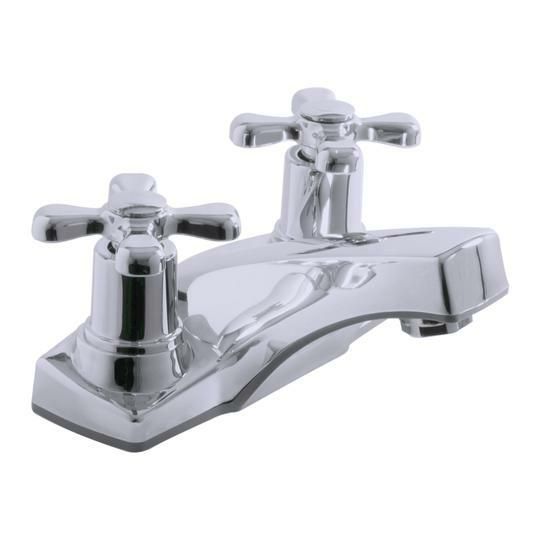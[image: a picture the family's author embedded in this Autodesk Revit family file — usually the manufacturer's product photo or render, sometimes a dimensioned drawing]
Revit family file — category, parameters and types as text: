
# Revit family: 01-1302-11 MEZCLADOR LAVAMANOS 4” ATLANTICO
name_source: partatom
category: Plumbing Fixtures
revit_build: Autodesk Revit 2018 (Build: 20170223_1515(x64)
units: mm (PartAtom-declared; Revit-internal decimal feet)

## family parameters
Cut with Voids When Loaded = No
Host = Face
OmniClass Number = 23.31.11.00
Part Type = Normal
Room Calculation Point = No
Round Connector Dimension = Use Diameter
Shared = No

## types (1)
- 01-1302-11
    Alto = 74.6 mm  [stored 0.244751 ft]
    CW Connection = Yes
    Default Elevation = 0 mm  [stored 0 ft]
    Description = Bimando baño
    Eje - Rosca = 101.6 mm
    Eje- Eje = 88 mm
    HW Connection = Yes
    Link Ficha Tecnica = https://infotecnica.gricol.com
    Manija = 66 mm  [stored 0.216535 ft]
    Manufacturer = Gricol
    Metal Laton Cromado = Metal Laton Cromado
    Model = 01-1302-11
    Plastico ABS Cromado = Plastico - ABS Cromado
    Product Name = MEZCLADOR LAVAMANOS 4” ATLANTICO
    Type Image = MEZCLADOR LAVAMANOS 4” ATLANTICO.jpg
    URL = https://www.gricol.com
    Vent Connection = No
    Waste Connection = No

note: [stored X ft] marks values corroborated as IEEE doubles in the binary element streams (Revit-internal decimal feet)

## geometry (parser evidence)
native form markers: Blend x2, Sweep x4
no freeform markers — native parametric forms only
